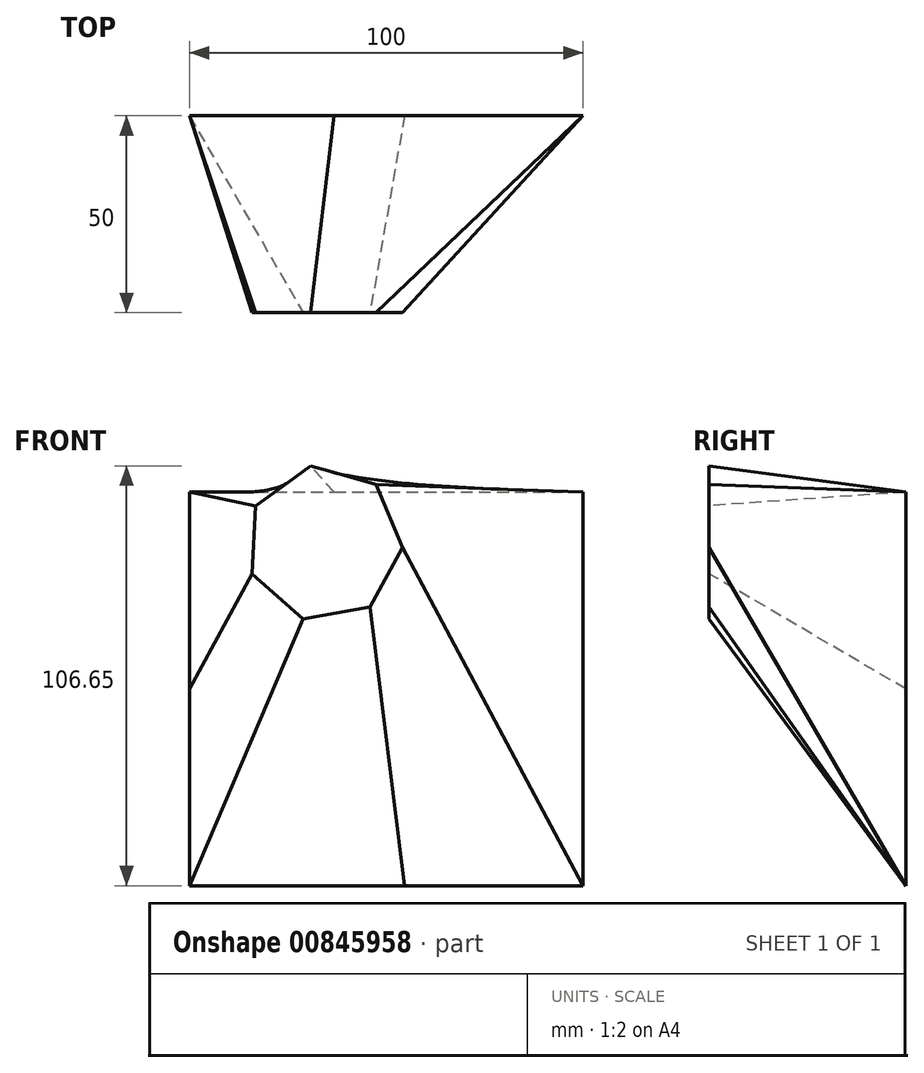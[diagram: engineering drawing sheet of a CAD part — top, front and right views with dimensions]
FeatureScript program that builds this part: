
annotation { "Feature Type Name" : "Feature", "Feature Type Description" : "" }
export const myFeature = defineFeature(function(context is Context, id is Id, definition is map)
    precondition{}
    {
        {
            var Q0;
            Q0=qCreatedBy(makeId("Front.planeOp"),FACE);
            var sketch = newSketch(context, id + "F0", { "sketchPlane" : qUnion([Q0]), "disableImprinting" : false});
            skLineSegment(sketch, "E0.bottom", {"start": v(-50, -50) * mm, "end": v(4.6, -50) * mm});
            skLineSegment(sketch, "E0.top", {"start": v(-50, 50) * mm, "end": v(-13.3, 50) * mm});
            skLineSegment(sketch, "E0.left", {"start": v(-50, -50) * mm, "end": v(-50, 50) * mm});
            skLineSegment(sketch, "E0.right", {"start": v(50, -50) * mm, "end": v(50, 50) * mm});
            skPoint(sketch, "E0.middle", {"position": v(0, 0) * mm});
            skLineSegment(sketch, "E1", {"start": v(-13.3, 50) * mm, "end": v(50, 50) * mm});
            skLineSegment(sketch, "E2", {"start": v(4.6, -50) * mm, "end": v(50, -50) * mm});
            skSolve(sketch);
        }
        {
            var Q0;
            Q0=qCreatedBy(makeId("Front.planeOp"),FACE);
            cPlane(context, id + "F1", {"entities" : qUnion([Q0]), "cplaneType" : CPlaneType.OFFSET, "offset" : 50 * mm, "width" : 150 * mm, "height" : 150 * mm});
        }
        {
            var Q0;
            Q0=qCreatedBy(id+"F1.planeOp",FACE);
            var sketch = newSketch(context, id + "F2", { "sketchPlane" : qUnion([Q0])});
            skCircle(sketch, "E3.cCircle", {"center": v(-15.77, 37) * mm, "radius": 17.97 * mm, "construction": true});
            skLineSegment(sketch, "E3.0", {"start": v(4.15, 35.99) * mm, "end": v(-4.15, 20.8) * mm});
            skLineSegment(sketch, "E3.1", {"start": v(-4.15, 20.8) * mm, "end": v(-21.2, 17.8) * mm});
            skLineSegment(sketch, "E3.2", {"start": v(-21.2, 17.8) * mm, "end": v(-34.16, 29.27) * mm});
            skLineSegment(sketch, "E3.3", {"start": v(-34.16, 29.27) * mm, "end": v(-33.28, 46.56) * mm});
            skLineSegment(sketch, "E3.4", {"start": v(-33.28, 46.56) * mm, "end": v(-19.22, 56.65) * mm});
            skLineSegment(sketch, "E3.5", {"start": v(-19.22, 56.65) * mm, "end": v(-2.56, 51.94) * mm});
            skLineSegment(sketch, "E3.6", {"start": v(-2.56, 51.94) * mm, "end": v(4.15, 35.99) * mm});
            skPoint(sketch, "E3.0.midPoint", {"position": v(0, 28.39) * mm});
            skSolve(sketch);
        }
        {
            var Q0;
            Q0=makeQuery(id+"F0.imprint","IMPRINT",FACE,{"disambiguationData":[TD([[makeQuery(id+"F0.imprint","IMPRINT",EDGE,{"derivedFrom":sQuery(id+"F0.wireOp",EDGE,"E0.bottom")}),1.0]])]});
            var Q1;
            Q1=makeQuery(id+"F2.imprint","IMPRINT",FACE,{"disambiguationData":[TD([[makeQuery(id+"F2.imprint","IMPRINT",EDGE,{"derivedFrom":sQuery(id+"F2.wireOp",EDGE,"E3.0")}),-1.0]])]});
            var Q2;
            Q2=sQuery(id+"F2.wireOp",VERTEX,"E3.4.end");
            loft(context, id + "F3", {"sheetProfilesArray" : [{ "sheetProfileEntities" : qUnion([Q0]) }, { "sheetProfileEntities" : qUnion([Q1]) }], "connections" : [{ "connectionEntities" : qUnion([Q2]), "connectionEdgeQueries" : qUnion([]), "connectionEdgeParameters" : [] }]});
        }
    });
